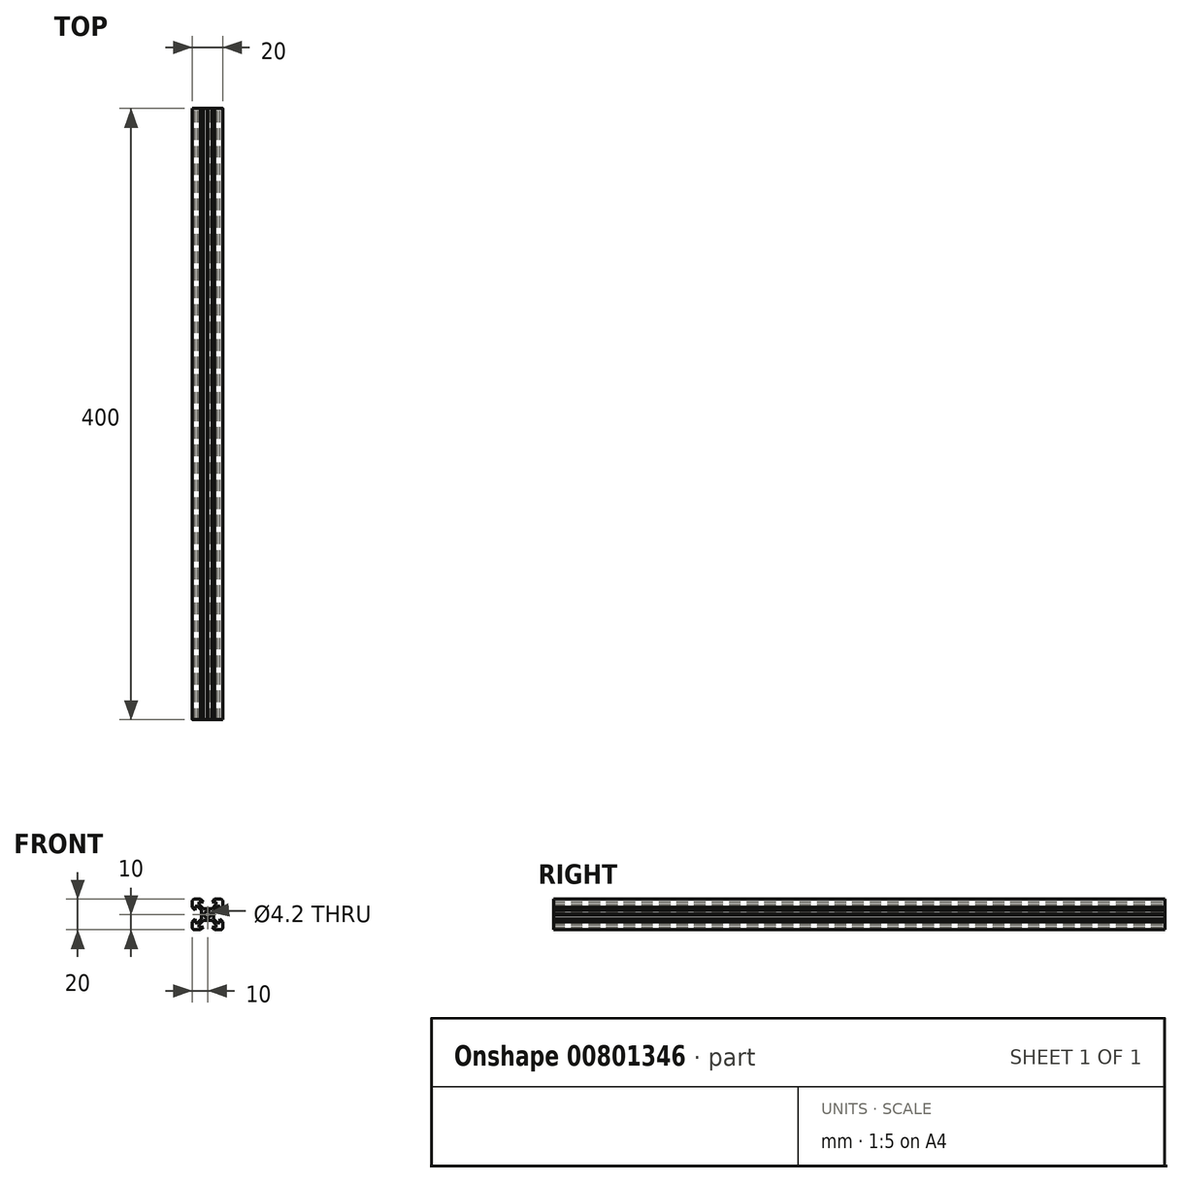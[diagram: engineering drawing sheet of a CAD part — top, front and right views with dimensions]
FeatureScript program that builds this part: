
annotation { "Feature Type Name" : "Feature", "Feature Type Description" : "" }
export const myFeature = defineFeature(function(context is Context, id is Id, definition is map)
    precondition{}
    {
        {
            var Q0;
            Q0=qCreatedBy(makeId("Front.planeOp"),FACE);
            var sketch = newSketch(context, id + "F0", { "sketchPlane" : qUnion([Q0])});
            skArc(sketch, "E0", {"start": v(-8.5, 10) * mm, "mid": v(-9.56, 9.56) * mm, "end": v(-10, 8.5) * mm});
            skLineSegment(sketch, "E1", {"start": v(-10, 8.5) * mm, "end": v(-10, 4.64) * mm});
            skLineSegment(sketch, "E2", {"start": v(-10, 4.64) * mm, "end": v(-8.2, 2.84) * mm});
            skLineSegment(sketch, "E3", {"start": v(-8.2, 5.5) * mm, "end": v(-8.2, 2.84) * mm});
            skLineSegment(sketch, "E4", {"start": v(-8.2, 5.5) * mm, "end": v(-6.56, 5.5) * mm});
            skLineSegment(sketch, "E5", {"start": v(-6.56, 5.5) * mm, "end": v(-3.9, 2.84) * mm});
            skLineSegment(sketch, "E6", {"start": v(-3.9, 2.84) * mm, "end": v(-3.9, 0.2) * mm});
            skLineSegment(sketch, "E7", {"start": v(-3.9, 0.2) * mm, "end": v(-3.7, 0) * mm});
            skLineSegment(sketch, "E8", {"start": v(-3.9, -0.2) * mm, "end": v(-3.7, 0) * mm});
            skLineSegment(sketch, "E9", {"start": v(-3.9, -2.84) * mm, "end": v(-3.9, -0.2) * mm});
            skLineSegment(sketch, "E10", {"start": v(-6.56, -5.5) * mm, "end": v(-3.9, -2.84) * mm});
            skLineSegment(sketch, "E11", {"start": v(-8.2, -5.5) * mm, "end": v(-6.56, -5.5) * mm});
            skLineSegment(sketch, "E12", {"start": v(-8.2, -5.5) * mm, "end": v(-8.2, -2.84) * mm});
            skLineSegment(sketch, "E13", {"start": v(-10, -4.64) * mm, "end": v(-8.2, -2.84) * mm});
            skLineSegment(sketch, "E14", {"start": v(-10, -8.5) * mm, "end": v(-10, -4.64) * mm});
            skArc(sketch, "E15", {"start": v(-10, -8.5) * mm, "mid": v(-9.56, -9.56) * mm, "end": v(-8.5, -10) * mm});
            skLineSegment(sketch, "E16", {"start": v(-8.5, -10) * mm, "end": v(-4.64, -10) * mm});
            skLineSegment(sketch, "E17", {"start": v(-4.64, -10) * mm, "end": v(-2.84, -8.2) * mm});
            skLineSegment(sketch, "E18", {"start": v(-2.84, -8.2) * mm, "end": v(-5.5, -8.2) * mm});
            skLineSegment(sketch, "E19", {"start": v(-5.5, -8.2) * mm, "end": v(-5.5, -6.56) * mm});
            skLineSegment(sketch, "E20", {"start": v(-5.5, -6.56) * mm, "end": v(-2.84, -3.9) * mm});
            skLineSegment(sketch, "E21", {"start": v(-0.2, -3.9) * mm, "end": v(-2.84, -3.9) * mm});
            skLineSegment(sketch, "E22", {"start": v(-0.2, -3.9) * mm, "end": v(0, -3.7) * mm});
            skLineSegment(sketch, "E23", {"start": v(0.2, -3.9) * mm, "end": v(0, -3.7) * mm});
            skLineSegment(sketch, "E24", {"start": v(0.2, -3.9) * mm, "end": v(2.84, -3.9) * mm});
            skLineSegment(sketch, "E25", {"start": v(5.5, -6.56) * mm, "end": v(2.84, -3.9) * mm});
            skLineSegment(sketch, "E26", {"start": v(5.5, -8.2) * mm, "end": v(5.5, -6.56) * mm});
            skLineSegment(sketch, "E27", {"start": v(2.84, -8.2) * mm, "end": v(5.5, -8.2) * mm});
            skLineSegment(sketch, "E28", {"start": v(4.64, -10) * mm, "end": v(2.84, -8.2) * mm});
            skLineSegment(sketch, "E29", {"start": v(8.5, -10) * mm, "end": v(4.64, -10) * mm});
            skArc(sketch, "E30", {"start": v(8.5, -10) * mm, "mid": v(9.56, -9.56) * mm, "end": v(10, -8.5) * mm});
            skLineSegment(sketch, "E31", {"start": v(10, -8.5) * mm, "end": v(10, -4.64) * mm});
            skLineSegment(sketch, "E32", {"start": v(10, -4.64) * mm, "end": v(8.2, -2.84) * mm});
            skLineSegment(sketch, "E33", {"start": v(8.2, -5.5) * mm, "end": v(8.2, -2.84) * mm});
            skLineSegment(sketch, "E34", {"start": v(8.2, -5.5) * mm, "end": v(6.56, -5.5) * mm});
            skLineSegment(sketch, "E35", {"start": v(6.56, -5.5) * mm, "end": v(3.9, -2.84) * mm});
            skLineSegment(sketch, "E36", {"start": v(3.9, -2.84) * mm, "end": v(3.9, -0.2) * mm});
            skLineSegment(sketch, "E37", {"start": v(3.9, -0.2) * mm, "end": v(3.7, 0) * mm});
            skLineSegment(sketch, "E38", {"start": v(3.9, 0.2) * mm, "end": v(3.7, 0) * mm});
            skLineSegment(sketch, "E39", {"start": v(3.9, 2.84) * mm, "end": v(3.9, 0.2) * mm});
            skLineSegment(sketch, "E40", {"start": v(6.56, 5.5) * mm, "end": v(3.9, 2.84) * mm});
            skLineSegment(sketch, "E41", {"start": v(8.2, 5.5) * mm, "end": v(6.56, 5.5) * mm});
            skLineSegment(sketch, "E42", {"start": v(8.2, 5.5) * mm, "end": v(8.2, 2.84) * mm});
            skLineSegment(sketch, "E43", {"start": v(10, 4.64) * mm, "end": v(8.2, 2.84) * mm});
            skLineSegment(sketch, "E44", {"start": v(10, 8.5) * mm, "end": v(10, 4.64) * mm});
            skArc(sketch, "E45", {"start": v(10, 8.5) * mm, "mid": v(9.56, 9.56) * mm, "end": v(8.5, 10) * mm});
            skLineSegment(sketch, "E46", {"start": v(8.5, 10) * mm, "end": v(4.64, 10) * mm});
            skLineSegment(sketch, "E47", {"start": v(4.64, 10) * mm, "end": v(2.84, 8.2) * mm});
            skLineSegment(sketch, "E48", {"start": v(2.84, 8.2) * mm, "end": v(5.5, 8.2) * mm});
            skLineSegment(sketch, "E49", {"start": v(5.5, 8.2) * mm, "end": v(5.5, 6.56) * mm});
            skLineSegment(sketch, "E50", {"start": v(5.5, 6.56) * mm, "end": v(2.84, 3.9) * mm});
            skLineSegment(sketch, "E51", {"start": v(0.2, 3.9) * mm, "end": v(2.84, 3.9) * mm});
            skLineSegment(sketch, "E52", {"start": v(0.2, 3.9) * mm, "end": v(0, 3.7) * mm});
            skLineSegment(sketch, "E53", {"start": v(-0.2, 3.9) * mm, "end": v(0, 3.7) * mm});
            skLineSegment(sketch, "E54", {"start": v(-0.2, 3.9) * mm, "end": v(-2.84, 3.9) * mm});
            skLineSegment(sketch, "E55", {"start": v(-5.5, 6.56) * mm, "end": v(-2.84, 3.9) * mm});
            skLineSegment(sketch, "E56", {"start": v(-5.5, 8.2) * mm, "end": v(-5.5, 6.56) * mm});
            skLineSegment(sketch, "E57", {"start": v(-2.84, 8.2) * mm, "end": v(-5.5, 8.2) * mm});
            skLineSegment(sketch, "E58", {"start": v(-4.64, 10) * mm, "end": v(-2.84, 8.2) * mm});
            skLineSegment(sketch, "E59", {"start": v(-8.5, 10) * mm, "end": v(-4.64, 10) * mm});
            skCircle(sketch, "E60", {"center": v(0, 0) * mm, "radius": 2.1 * mm});
            skSolve(sketch);
        }
        {
            var Q0;
            Q0=qSketchRegion(id+"F0",true);
            extrude(context, id + "F1", {"entities" : qUnion([Q0]), "endBound" : BoundingType.SYMMETRIC, "depth" : 400 * mm, "offsetDistance" : 25.4 * mm});
        }
        {
            var Q0;
            Q0=makeQuery(id+"F1.opExtrude","SWEPT_BODY",BODY,{"disambiguationData":[OSD([sQuery(id+"F0.wireOp",EDGE,"E0"),sQuery(id+"F0.wireOp",EDGE,"E1"),sQuery(id+"F0.wireOp",EDGE,"E2"),sQuery(id+"F0.wireOp",EDGE,"E3"),sQuery(id+"F0.wireOp",EDGE,"E4"),sQuery(id+"F0.wireOp",EDGE,"E5"),sQuery(id+"F0.wireOp",EDGE,"E6"),sQuery(id+"F0.wireOp",EDGE,"E7"),sQuery(id+"F0.wireOp",EDGE,"E8"),sQuery(id+"F0.wireOp",EDGE,"E9"),sQuery(id+"F0.wireOp",EDGE,"E10"),sQuery(id+"F0.wireOp",EDGE,"E11"),sQuery(id+"F0.wireOp",EDGE,"E12"),sQuery(id+"F0.wireOp",EDGE,"E13"),sQuery(id+"F0.wireOp",EDGE,"E14"),sQuery(id+"F0.wireOp",EDGE,"E15"),sQuery(id+"F0.wireOp",EDGE,"E16"),sQuery(id+"F0.wireOp",EDGE,"E17"),sQuery(id+"F0.wireOp",EDGE,"E18"),sQuery(id+"F0.wireOp",EDGE,"E19"),sQuery(id+"F0.wireOp",EDGE,"E20"),sQuery(id+"F0.wireOp",EDGE,"E21"),sQuery(id+"F0.wireOp",EDGE,"E22"),sQuery(id+"F0.wireOp",EDGE,"E23"),sQuery(id+"F0.wireOp",EDGE,"E24"),sQuery(id+"F0.wireOp",EDGE,"E25"),sQuery(id+"F0.wireOp",EDGE,"E26"),sQuery(id+"F0.wireOp",EDGE,"E27"),sQuery(id+"F0.wireOp",EDGE,"E28"),sQuery(id+"F0.wireOp",EDGE,"E29"),sQuery(id+"F0.wireOp",EDGE,"E30"),sQuery(id+"F0.wireOp",EDGE,"E31"),sQuery(id+"F0.wireOp",EDGE,"E32"),sQuery(id+"F0.wireOp",EDGE,"E33"),sQuery(id+"F0.wireOp",EDGE,"E34"),sQuery(id+"F0.wireOp",EDGE,"E35"),sQuery(id+"F0.wireOp",EDGE,"E36"),sQuery(id+"F0.wireOp",EDGE,"E37"),sQuery(id+"F0.wireOp",EDGE,"E38"),sQuery(id+"F0.wireOp",EDGE,"E39"),sQuery(id+"F0.wireOp",EDGE,"E40"),sQuery(id+"F0.wireOp",EDGE,"E41"),sQuery(id+"F0.wireOp",EDGE,"E42"),sQuery(id+"F0.wireOp",EDGE,"E43"),sQuery(id+"F0.wireOp",EDGE,"E44"),sQuery(id+"F0.wireOp",EDGE,"E45"),sQuery(id+"F0.wireOp",EDGE,"E46"),sQuery(id+"F0.wireOp",EDGE,"E47"),sQuery(id+"F0.wireOp",EDGE,"E48"),sQuery(id+"F0.wireOp",EDGE,"E49"),sQuery(id+"F0.wireOp",EDGE,"E50"),sQuery(id+"F0.wireOp",EDGE,"E51"),sQuery(id+"F0.wireOp",EDGE,"E52"),sQuery(id+"F0.wireOp",EDGE,"E53"),sQuery(id+"F0.wireOp",EDGE,"E54"),sQuery(id+"F0.wireOp",EDGE,"E55"),sQuery(id+"F0.wireOp",EDGE,"E56"),sQuery(id+"F0.wireOp",EDGE,"E57"),sQuery(id+"F0.wireOp",EDGE,"E58"),sQuery(id+"F0.wireOp",EDGE,"E59"),sQuery(id+"F0.wireOp",EDGE,"E60")])]});
            var Q1;
            Q1=makeQuery(id+"F1.opExtrude","SWEPT_EDGE",EDGE,{"disambiguationData":[OSD([sQuery(id+"F0.wireOp",EDGE,"E0"),sQuery(id+"F0.wireOp",EDGE,"E59")])]});
            transform(context, id + "F2", {"entities" : qUnion([Q0]), "transformType" : TransformType.TRANSLATION_DISTANCE, "transformDirection" : qUnion([Q1]), "distance" : 200 * mm, "makeCopy" : false});
        }
    });
